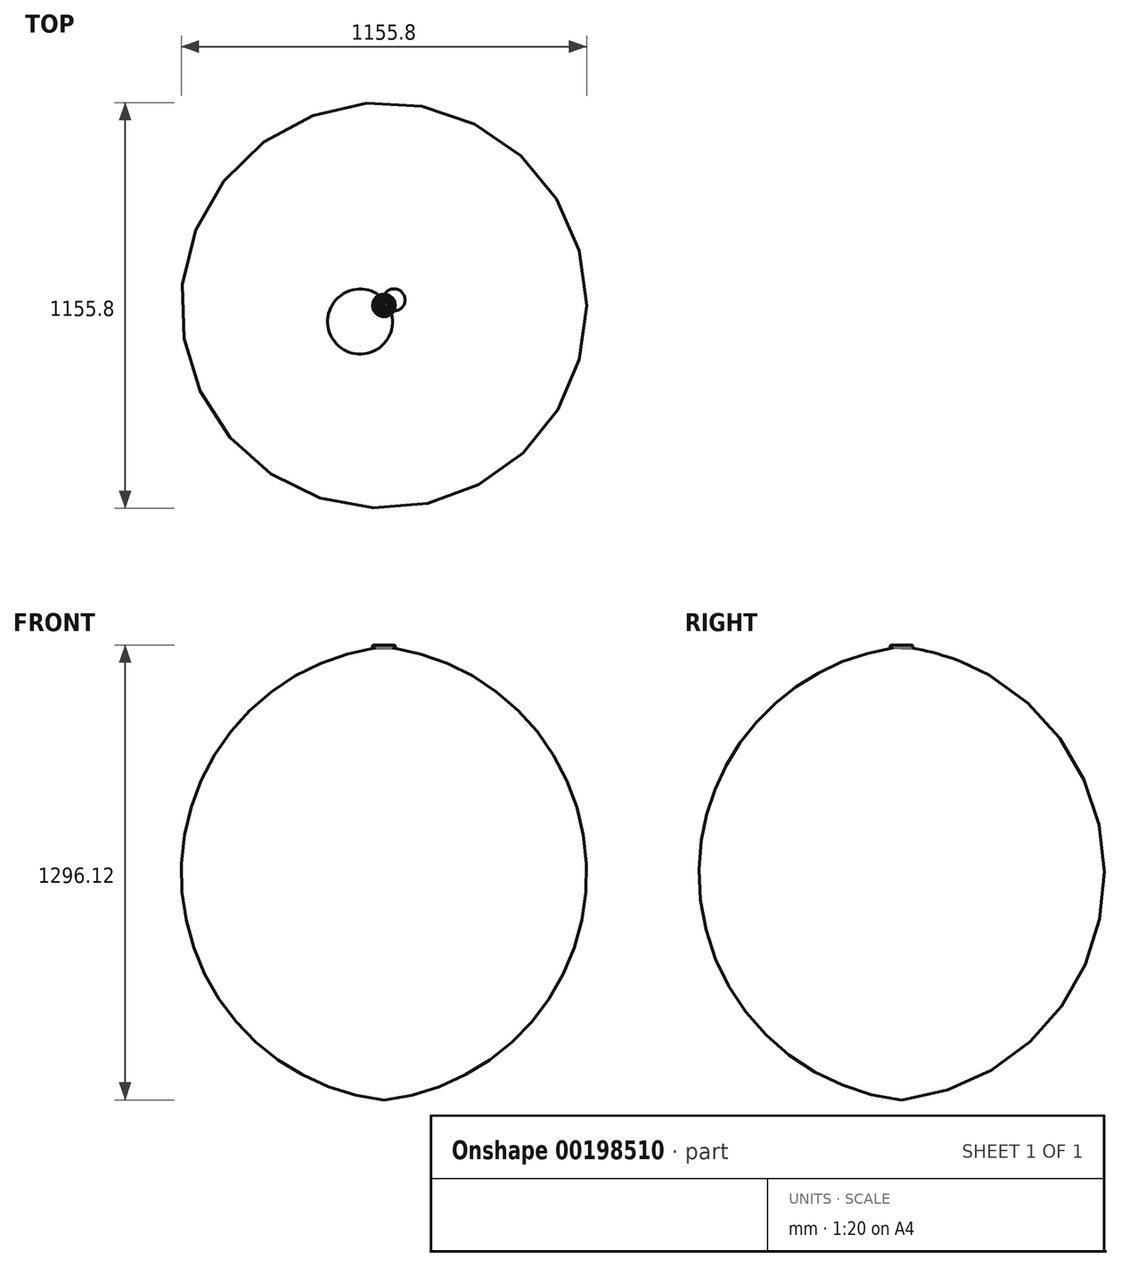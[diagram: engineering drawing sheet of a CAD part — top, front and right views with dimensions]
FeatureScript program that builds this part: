
annotation { "Feature Type Name" : "Feature", "Feature Type Description" : "" }
export const myFeature = defineFeature(function(context is Context, id is Id, definition is map)
    precondition{}
    {
        {
            var Q0;
            Q0=qCreatedBy(makeId("Front.planeOp"),FACE);
            var sketch = newSketch(context, id + "F0", { "sketchPlane" : qUnion([Q0])});
            skArc(sketch, "E0", {"start": v(-29.38, 9.94) * mm, "mid": v(-31.55, 9.3) * mm, "end": v(-31.73, 7.04) * mm});
            skArc(sketch, "E1", {"start": v(-31.73, 3.04) * mm, "mid": v(-31.73, 1.04) * mm, "end": v(-30, 0.04) * mm});
            skLineSegment(sketch, "E2", {"start": v(0, 0) * mm, "end": v(-30, 0.04) * mm});
            skLineSegment(sketch, "E3", {"start": v(0, 0) * mm, "end": v(0, 5.29) * mm});
            skArc(sketch, "E4", {"start": v(-31.73, 7.04) * mm, "mid": v(-32.36, 5.04) * mm, "end": v(-31.73, 3.04) * mm});
            skArc(sketch, "E5", {"start": v(-29.38, 9.94) * mm, "mid": v(-24, 7.7) * mm, "end": v(-18.2, 7.05) * mm});
            skArc(sketch, "E6", {"start": v(0, 5.29) * mm, "mid": v(-9.1, 6.23) * mm, "end": v(-18.2, 7.05) * mm});
            skPoint(sketch, "E7.center.orphan", {"position": v(0, 100.29) * mm});
            skSolve(sketch);
        }
        {
            var Q0;
            Q0=qCreatedBy(makeId("Top.planeOp"),FACE);
            cPlane(context, id + "F1", {"entities" : qUnion([Q0]), "cplaneType" : CPlaneType.OFFSET, "offset" : 5.27 * mm, "width" : 150 * mm, "height" : 150 * mm});
        }
        {
            var Q0;
            Q0=qCreatedBy(id+"F1.planeOp",FACE);
            var sketch = newSketch(context, id + "F2", { "sketchPlane" : qUnion([Q0])});
            skCircle(sketch, "E8", {"center": v(0, 0) * mm, "radius": 21.32 * mm});
            skCircle(sketch, "E9", {"center": v(0, 0) * mm, "radius": 23.95 * mm});
            skLineSegment(sketch, "E10", {"start": v(-5.89, 15.8) * mm, "end": v(6.25, 15.8) * mm});
            skLineSegment(sketch, "E11", {"start": v(-16.79, -6.28) * mm, "end": v(-9.61, -14.63) * mm});
            skLineSegment(sketch, "E12", {"start": v(14.88, -7.73) * mm, "end": v(7.84, -16.14) * mm});
            skArc(sketch, "E13", {"start": v(-5.89, 15.8) * mm, "mid": v(-13.26, 5.7) * mm, "end": v(-16.79, -6.28) * mm});
            skArc(sketch, "E14", {"start": v(6.25, 15.8) * mm, "mid": v(-5.57, 2.61) * mm, "end": v(-9.61, -14.63) * mm});
            skArc(sketch, "E15", {"start": v(-9.61, -14.63) * mm, "mid": v(-1.02, -16.92) * mm, "end": v(7.84, -16.14) * mm});
            skFitSpline(sketch, "E16", {"points": [v(6.25, 15.8) * mm, v(14.88, -7.73) * mm], "startDerivative": vector(-4.6, -24.48) * mm, "endDerivative": vector(0.4, -25.4) * mm});
            skFitSpline(sketch, "E17", {"points": [v(-1.4, 8.88) * mm, v(7.84, -16.14) * mm], "startDerivative": vector(0.8, -26.64) * mm, "endDerivative": vector(-3.13, -27.2) * mm});
            skArc(sketch, "E18", {"start": v(-9.06, -7.63) * mm, "mid": v(-1.3, -9.7) * mm, "end": v(6.74, -9.31) * mm});
            skLineSegment(sketch, "E19.bottom", {"start": v(-5.8, 27) * mm, "end": v(-4.63, 27) * mm});
            skLineSegment(sketch, "E19.top", {"start": v(-5.8, -26.81) * mm, "end": v(-4.63, -26.81) * mm});
            skLineSegment(sketch, "E19.left", {"start": v(-5.8, 27) * mm, "end": v(-5.8, 23.24) * mm});
            skLineSegment(sketch, "E19.right", {"start": v(-4.63, 27) * mm, "end": v(-4.63, 23.5) * mm});
            skLineSegment(sketch, "E20.bottom", {"start": v(-27.25, 2.38) * mm, "end": v(-23.83, 2.38) * mm});
            skLineSegment(sketch, "E20.top", {"start": v(-27.25, 1.45) * mm, "end": v(-23.9, 1.45) * mm});
            skLineSegment(sketch, "E20.left", {"start": v(-27.25, 2.38) * mm, "end": v(-27.25, 1.45) * mm});
            skLineSegment(sketch, "E20.right", {"start": v(27.97, 2.38) * mm, "end": v(27.97, 1.45) * mm});
            skLineSegment(sketch, "E21.trimOffspring", {"start": v(-5.8, 20.52) * mm, "end": v(-5.8, 15.8) * mm});
            skLineSegment(sketch, "E22.trimOffspring", {"start": v(-4.63, 20.8) * mm, "end": v(-4.63, 15.8) * mm});
            skLineSegment(sketch, "E23.trimOffspring", {"start": v(-21.27, 1.45) * mm, "end": v(-15.03, 1.45) * mm});
            skLineSegment(sketch, "E24.trimOffspring", {"start": v(-21.19, 2.38) * mm, "end": v(-14.7, 2.38) * mm});
            skLineSegment(sketch, "E25.trimOffspring", {"start": v(-6.15, 1.45) * mm, "end": v(-5.8, 1.45) * mm});
            skLineSegment(sketch, "E26.trimOffspring", {"start": v(-4.63, 4.3) * mm, "end": v(-4.63, 2.38) * mm});
            skLineSegment(sketch, "E27.trimOffspring", {"start": v(-4.63, 1.45) * mm, "end": v(-4.63, -9.13) * mm});
            skLineSegment(sketch, "E28.trimOffspring", {"start": v(-4.63, 2.38) * mm, "end": v(0.35, 2.38) * mm});
            skLineSegment(sketch, "E29.trimOffspring", {"start": v(-4.63, 1.45) * mm, "end": v(0.81, 1.45) * mm});
            skLineSegment(sketch, "E30.trimOffspring", {"start": v(-5.8, 1.45) * mm, "end": v(-5.8, -8.82) * mm});
            skLineSegment(sketch, "E31.trimOffspring", {"start": v(11.59, 1.45) * mm, "end": v(21.27, 1.45) * mm});
            skLineSegment(sketch, "E32.trimOffspring", {"start": v(11.03, 2.38) * mm, "end": v(21.19, 2.38) * mm});
            skLineSegment(sketch, "E33.trimOffspring", {"start": v(23.83, 2.38) * mm, "end": v(27.97, 2.38) * mm});
            skLineSegment(sketch, "E34.trimOffspring", {"start": v(23.9, 1.45) * mm, "end": v(27.97, 1.45) * mm});
            skLineSegment(sketch, "E35.trimOffspring", {"start": v(-5.8, -23.24) * mm, "end": v(-5.8, -26.81) * mm});
            skLineSegment(sketch, "E36.trimOffspring", {"start": v(-4.63, -23.5) * mm, "end": v(-4.63, -26.81) * mm});
            skLineSegment(sketch, "E37.trimOffspring", {"start": v(-4.63, -16.34) * mm, "end": v(-4.63, -20.8) * mm});
            skLineSegment(sketch, "E38.trimOffspring", {"start": v(-5.8, -16.04) * mm, "end": v(-5.8, -20.52) * mm});
            skSolve(sketch);
        }
        {
            var Q0;
            {var subQ7=sQuery(id+"F2.wireOp",EDGE,"E11");Q0=makeQuery(id+"F2.imprint","IMPRINT",FACE,{"disambiguationData":[TD([[makeQuery(id+"F2.imprint","IMPRINT",EDGE,{"derivedFrom":subQ7}),1.0]])]});}
            extrude(context, id + "F3", {"entities" : qUnion([Q0]), "depth" : 5 * mm});
        }
        {
            var Q0;
            {var subQ7=sQuery(id+"F2.wireOp",EDGE,"E12");Q0=makeQuery(id+"F2.imprint","IMPRINT",FACE,{"disambiguationData":[TD([[makeQuery(id+"F2.imprint","IMPRINT",EDGE,{"derivedFrom":subQ7}),-1.0]])]});}
            extrude(context, id + "F4", {"entities" : qUnion([Q0]), "operationType" : NewBodyOperationType.ADD, "depth" : 4 * mm});
        }
        {
            var Q0;
            {var subQ1=sQuery(id+"F2.wireOp",EDGE,"E15");var subQ3=makeQuery(id+"F2.imprint","INTERSECT",VERTEX,{"derivedFrom":[subQ1,sQuery(id+"F2.wireOp",EDGE,"E37.trimOffspring")]});Q0=makeQuery(id+"F2.imprint","IMPRINT",FACE,{"disambiguationData":[TD([[makeQuery(id+"F2.imprint","IMPRINT",EDGE,{"disambiguationData":[TD([[subQ3,1.0]])],"derivedFrom":subQ1}),1.0]])]});}
            extrude(context, id + "F5", {"entities" : qUnion([Q0]), "operationType" : NewBodyOperationType.ADD, "depth" : 3 * mm});
        }
        {
            var Q0;
            {var subQ3=sQuery(id+"F2.wireOp",EDGE,"E8");var subQ4=makeQuery(id+"F2.imprint","INTERSECT",VERTEX,{"derivedFrom":[subQ3,sQuery(id+"F2.wireOp",EDGE,"E31.trimOffspring")]});Q0=makeQuery(id+"F2.imprint","IMPRINT",FACE,{"disambiguationData":[TD([[makeQuery(id+"F2.imprint","IMPRINT",EDGE,{"disambiguationData":[TD([[subQ4,-1.0]])],"derivedFrom":subQ3}),-1.0]])]});}
            extrude(context, id + "F6", {"entities" : qUnion([Q0]), "depth" : 5 * mm});
        }
        {
            var Q0;
            {var subQ0=sQuery(id+"F2.wireOp",EDGE,"E20.bottom");Q0=makeQuery(id+"F2.imprint","IMPRINT",FACE,{"disambiguationData":[TD([[makeQuery(id+"F2.imprint","IMPRINT",EDGE,{"derivedFrom":subQ0}),-1.0]])]});}
            var Q1;
            Q1=makeQuery(id+"F2.imprint","IMPRINT",FACE,{"disambiguationData":[TD([[makeQuery(id+"F2.imprint","IMPRINT",EDGE,{"derivedFrom":sQuery(id+"F2.wireOp",EDGE,"E19.bottom")}),-1.0]])]});
            var Q2;
            Q2=makeQuery(id+"F2.imprint","IMPRINT",FACE,{"disambiguationData":[TD([[makeQuery(id+"F2.imprint","IMPRINT",EDGE,{"derivedFrom":sQuery(id+"F2.wireOp",EDGE,"E20.right")}),-1.0]])]});
            var Q3;
            Q3=makeQuery(id+"F2.imprint","IMPRINT",FACE,{"disambiguationData":[TD([[makeQuery(id+"F2.imprint","IMPRINT",EDGE,{"derivedFrom":sQuery(id+"F2.wireOp",EDGE,"E19.top")}),1.0]])]});
            var Q4;
            {var subQ0=sQuery(id+"F2.wireOp",EDGE,"E25.trimOffspring");Q4=makeQuery(id+"F2.imprint","IMPRINT",FACE,{"disambiguationData":[TD([[makeQuery(id+"F2.imprint","IMPRINT",EDGE,{"derivedFrom":subQ0}),1.0]])]});}
            var Q5;
            {var subQ0=sQuery(id+"F2.wireOp",EDGE,"E23.trimOffspring");Q5=makeQuery(id+"F2.imprint","IMPRINT",FACE,{"disambiguationData":[TD([[makeQuery(id+"F2.imprint","IMPRINT",EDGE,{"derivedFrom":subQ0}),1.0]])]});}
            var Q6;
            {var subQ0=sQuery(id+"F2.wireOp",EDGE,"E21.trimOffspring");Q6=makeQuery(id+"F2.imprint","IMPRINT",FACE,{"disambiguationData":[TD([[makeQuery(id+"F2.imprint","IMPRINT",EDGE,{"derivedFrom":subQ0}),1.0]])]});}
            var Q7;
            {var subQ0=sQuery(id+"F2.wireOp",EDGE,"E31.trimOffspring");Q7=makeQuery(id+"F2.imprint","IMPRINT",FACE,{"disambiguationData":[TD([[makeQuery(id+"F2.imprint","IMPRINT",EDGE,{"derivedFrom":subQ0}),1.0]])]});}
            var Q8;
            {var subQ0=sQuery(id+"F2.wireOp",EDGE,"E37.trimOffspring");Q8=makeQuery(id+"F2.imprint","IMPRINT",FACE,{"disambiguationData":[TD([[makeQuery(id+"F2.imprint","IMPRINT",EDGE,{"derivedFrom":subQ0}),-1.0]])]});}
            extrude(context, id + "F7", {"entities" : qUnion([Q0, Q1, Q2, Q3, Q4, Q5, Q6, Q7, Q8]), "depth" : 2 * mm});
        }
        {
            var Q0;
            Q0=makeQuery(id+"F0.imprint","IMPRINT",FACE,{"disambiguationData":[TD([[makeQuery(id+"F0.imprint","IMPRINT",EDGE,{"derivedFrom":sQuery(id+"F0.wireOp",EDGE,"E0")}),1.0]])]});
            var Q1;
            Q1=sQuery(id+"F0.wireOp",EDGE,"E3");
            revolve(context, id + "F8", {"entities" : qUnion([Q0]), "axis" : qUnion([Q1]), "revolveType" : RevolveType.FULL});
        }
        {
            var Q0;
            Q0=makeQuery(id+"F8.opRevolve","SWEPT_FACE",FACE,{"disambiguationData":[OSD([sQuery(id+"F0.wireOp",EDGE,"E4")])]});
            fillet(context, id + "F9", {"entities" : qUnion([Q0]), "radius" : 5 * mm, "tangentPropagation" : true, "allowEdgeOverflow" : false});
        }
        {
            var Q0;
            Q0=qCreatedBy(makeId("Top.planeOp"),FACE);
            var sketch = newSketch(context, id + "F10", { "sketchPlane" : qUnion([Q0])});
            skCircle(sketch, "E39", {"center": v(0, 34.68) * mm, "radius": 4.04 * mm});
            skSolve(sketch);
        }
        {
            var Q0;
            Q0=makeQuery(id+"F10.imprint","IMPRINT",FACE,{"disambiguationData":[TD([[makeQuery(id+"F10.imprint","IMPRINT",EDGE,{"derivedFrom":sQuery(id+"F10.wireOp",EDGE,"E39")}),1.0]])]});
            extrude(context, id + "F11", {"entities" : qUnion([Q0]), "operationType" : NewBodyOperationType.REMOVE, "depth" : 25 * mm});
        }
        {
            var Q0;
            Q0=makeQuery(id+"F11.boolean.opBoolean","INTERSECT",EDGE,{"derivedFrom":[makeQuery(id+"F8.opRevolve","SWEPT_FACE",FACE,{"disambiguationData":[OSD([sQuery(id+"F0.wireOp",EDGE,"E0")])]}),makeQuery(id+"F11.opExtrude","SWEPT_FACE",FACE,{"disambiguationData":[OSD([sQuery(id+"F10.wireOp",EDGE,"E39")])]})]});
            var Q1;
            Q1=makeQuery(id+"F11.boolean.opBoolean","INTERSECT",EDGE,{"disambiguationData":[OD(0.0)],"derivedFrom":[makeQuery(id+"F9.opFillet","BLEND_FACE",FACE,{"disambiguationData":[OSD([sQuery(id+"F0.wireOp",EDGE,"E0"),sQuery(id+"F0.wireOp",EDGE,"E4")])]}),makeQuery(id+"F11.opExtrude","SWEPT_FACE",FACE,{"disambiguationData":[OSD([sQuery(id+"F10.wireOp",EDGE,"E39")])]})]});
            var Q2;
            Q2=makeQuery(id+"F11.boolean.opBoolean","INTERSECT",EDGE,{"disambiguationData":[OD(0.0)],"derivedFrom":[makeQuery(id+"F8.opRevolve","SWEPT_FACE",FACE,{"disambiguationData":[OSD([sQuery(id+"F0.wireOp",EDGE,"E4")])]}),makeQuery(id+"F11.opExtrude","SWEPT_FACE",FACE,{"disambiguationData":[OSD([sQuery(id+"F10.wireOp",EDGE,"E39")])]})]});
            var Q3;
            Q3=makeQuery(id+"F11.boolean.opBoolean","INTERSECT",EDGE,{"disambiguationData":[OD(0.0)],"derivedFrom":[makeQuery(id+"F9.opFillet","BLEND_FACE",FACE,{"disambiguationData":[OSD([sQuery(id+"F0.wireOp",EDGE,"E1"),sQuery(id+"F0.wireOp",EDGE,"E4")])]}),makeQuery(id+"F11.opExtrude","SWEPT_FACE",FACE,{"disambiguationData":[OSD([sQuery(id+"F10.wireOp",EDGE,"E39")])]})]});
            var Q4;
            Q4=makeQuery(id+"F11.boolean.opBoolean","INTERSECT",EDGE,{"derivedFrom":[makeQuery(id+"F8.opRevolve","SWEPT_FACE",FACE,{"disambiguationData":[OSD([sQuery(id+"F0.wireOp",EDGE,"E1")])]}),makeQuery(id+"F11.opExtrude","SWEPT_FACE",FACE,{"disambiguationData":[OSD([sQuery(id+"F10.wireOp",EDGE,"E39")])]})]});
            var Q5;
            Q5=makeQuery(id+"F11.boolean.opBoolean","INTERSECT",EDGE,{"disambiguationData":[OD(1.0)],"derivedFrom":[makeQuery(id+"F8.opRevolve","SWEPT_FACE",FACE,{"disambiguationData":[OSD([sQuery(id+"F0.wireOp",EDGE,"E4")])]}),makeQuery(id+"F11.opExtrude","SWEPT_FACE",FACE,{"disambiguationData":[OSD([sQuery(id+"F10.wireOp",EDGE,"E39")])]})]});
            var Q6;
            Q6=makeQuery(id+"F11.boolean.opBoolean","INTERSECT",EDGE,{"disambiguationData":[OD(1.0)],"derivedFrom":[makeQuery(id+"F9.opFillet","BLEND_FACE",FACE,{"disambiguationData":[OSD([sQuery(id+"F0.wireOp",EDGE,"E0"),sQuery(id+"F0.wireOp",EDGE,"E4")])]}),makeQuery(id+"F11.opExtrude","SWEPT_FACE",FACE,{"disambiguationData":[OSD([sQuery(id+"F10.wireOp",EDGE,"E39")])]})]});
            fillet(context, id + "F12", {"entities" : qUnion([Q0, Q1, Q2, Q3, Q4, Q5, Q6]), "radius" : 0.5 * mm, "tangentPropagation" : true, "allowEdgeOverflow" : false});
        }
    });
